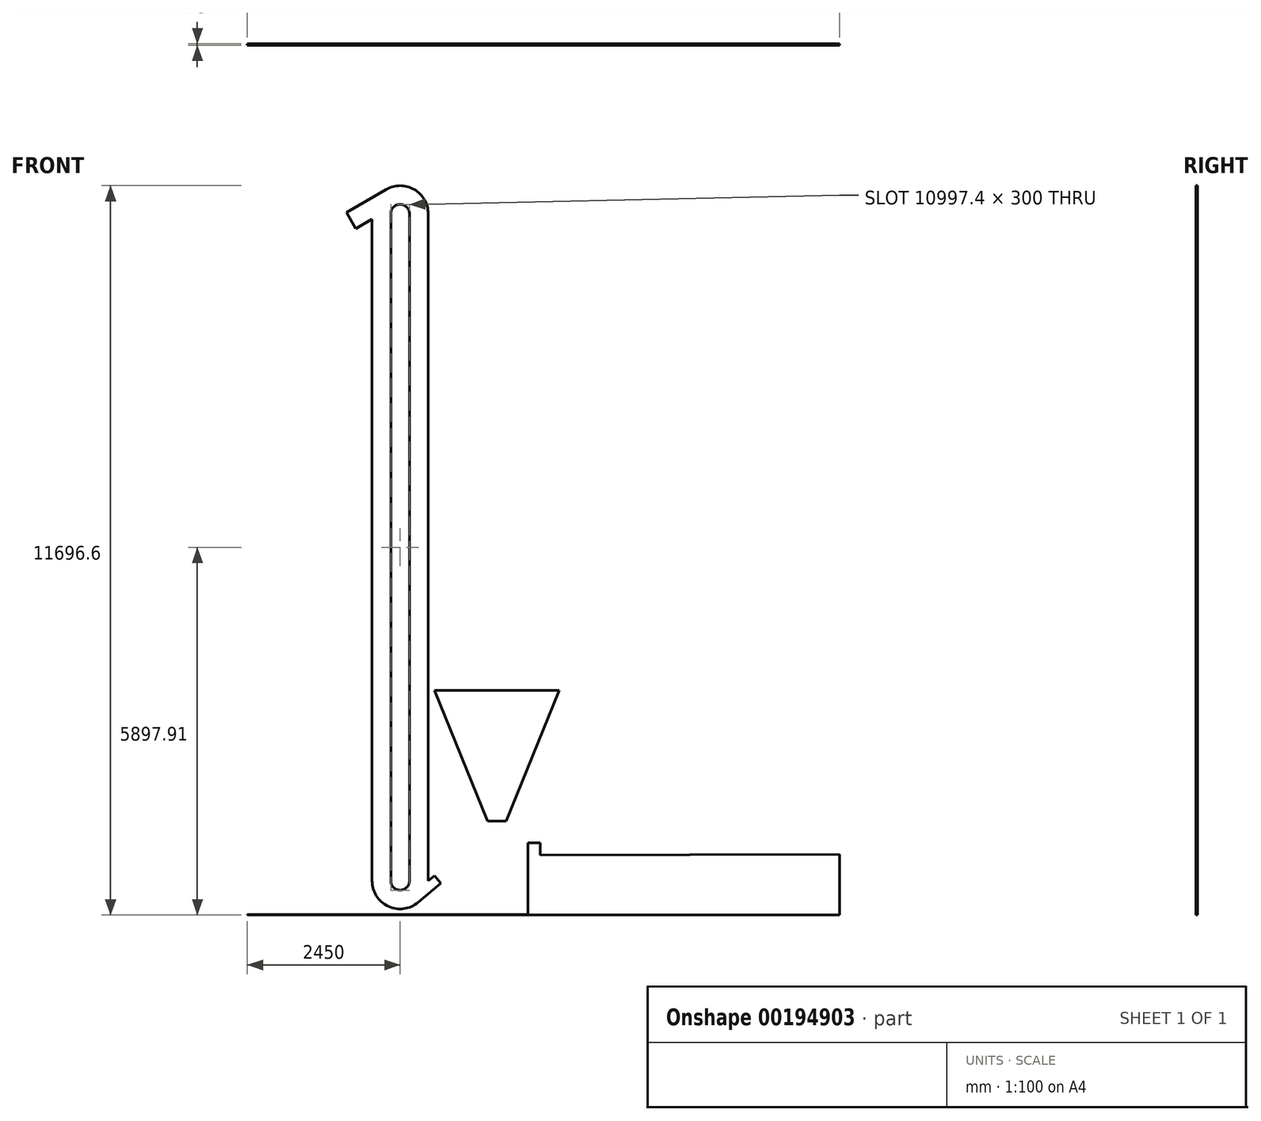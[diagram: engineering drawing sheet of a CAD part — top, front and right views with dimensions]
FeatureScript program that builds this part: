
annotation { "Feature Type Name" : "Feature", "Feature Type Description" : "" }
export const myFeature = defineFeature(function(context is Context, id is Id, definition is map)
    precondition{}
    {
        {
            var Q0;
            Q0=qCreatedBy(makeId("Front.planeOp"),FACE);
            var sketch = newSketch(context, id + "F0", { "sketchPlane" : qUnion([Q0])});
            skLineSegment(sketch, "E0", {"start": v(0, 3590) * mm, "end": v(850, 1500) * mm});
            skLineSegment(sketch, "E1", {"start": v(850, 1500) * mm, "end": v(1150, 1500) * mm});
            skLineSegment(sketch, "E2", {"start": v(1150, 1500) * mm, "end": v(2000, 3590) * mm});
            skLineSegment(sketch, "E3", {"start": v(2000, 3590) * mm, "end": v(0, 3590) * mm});
            skLineSegment(sketch, "E4", {"start": v(-3000, 0) * mm, "end": v(1500, 0) * mm});
            skLineSegment(sketch, "E5", {"start": v(-100, 11236.6) * mm, "end": v(-100, 539.23) * mm});
            skLineSegment(sketch, "E6", {"start": v(-100, 539.23) * mm, "end": v(0, 623.14) * mm});
            skLineSegment(sketch, "E7", {"start": v(0, 623.14) * mm, "end": v(103.33, 500) * mm});
            skLineSegment(sketch, "E8", {"start": v(103.33, 500) * mm, "end": v(-260.75, 194.5) * mm});
            skLineSegment(sketch, "E9", {"start": v(-1000, 539.23) * mm, "end": v(-1000, 11236.6) * mm});
            skArc(sketch, "E10", {"start": v(-260.75, 194.5) * mm, "mid": v(-740.18, 131.39) * mm, "end": v(-1000, 539.23) * mm});
            skArc(sketch, "E11", {"start": v(-400, 539.23) * mm, "mid": v(-550, 389.23) * mm, "end": v(-700, 539.23) * mm});
            skLineSegment(sketch, "E12", {"start": v(-700, 539.23) * mm, "end": v(-700, 11236.6) * mm});
            skLineSegment(sketch, "E13", {"start": v(-400, 539.23) * mm, "end": v(-400, 11236.6) * mm});
            skLineSegment(sketch, "E14", {"start": v(1497.05, 1150) * mm, "end": v(1697.05, 1150.51) * mm});
            skLineSegment(sketch, "E15", {"start": v(1697.05, 1150.51) * mm, "end": v(1697.56, 950.51) * mm});
            skLineSegment(sketch, "E16", {"start": v(1697.56, 950.51) * mm, "end": v(6497.55, 962.84) * mm});
            skLineSegment(sketch, "E17", {"start": v(6497.55, 962.84) * mm, "end": v(6500.02, 0) * mm});
            skLineSegment(sketch, "E18", {"start": v(1497.05, 1150) * mm, "end": v(1500, 0) * mm});
            skArc(sketch, "E19", {"start": v(-775, 11626.31) * mm, "mid": v(-325, 11626.31) * mm, "end": v(-100, 11236.6) * mm});
            skArc(sketch, "E20", {"start": v(-700, 11236.6) * mm, "mid": v(-550, 11386.6) * mm, "end": v(-400, 11236.6) * mm});
            skLineSegment(sketch, "E21", {"start": v(-775, 11626.31) * mm, "end": v(-1409.8, 11259.8) * mm});
            skLineSegment(sketch, "E22", {"start": v(-1409.8, 11259.8) * mm, "end": v(-1259.8, 11000) * mm});
            skLineSegment(sketch, "E23", {"start": v(-1259.8, 11000) * mm, "end": v(-1000, 11150) * mm});
            skLineSegment(sketch, "E24", {"start": v(-3000, 0) * mm, "end": v(-3000, -10) * mm});
            skLineSegment(sketch, "E25", {"start": v(-3000, -10) * mm, "end": v(6500.02, -10) * mm});
            skLineSegment(sketch, "E26", {"start": v(6500.02, 0) * mm, "end": v(6500.02, -10) * mm});
            skLineSegment(sketch, "E27", {"start": v(244.02, 2990) * mm, "end": v(1755.98, 2990) * mm});
            skSolve(sketch);
        }
        {
            var Q0;
            Q0=qSketchRegion(id+"F0",true);
            extrude(context, id + "F1", {"entities" : qUnion([Q0]), "depth" : 25 * mm});
        }
    });
